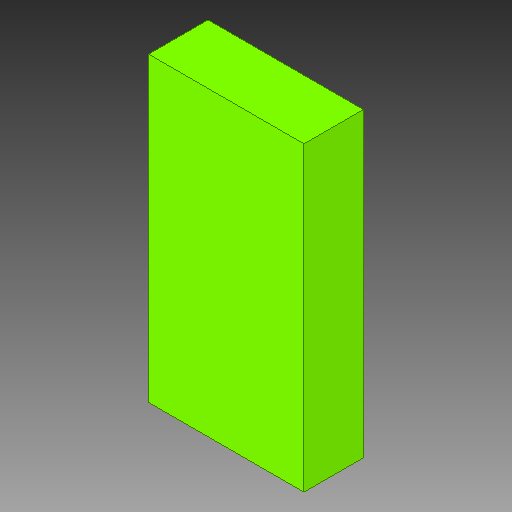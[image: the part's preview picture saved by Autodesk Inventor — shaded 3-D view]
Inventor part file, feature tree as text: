
AUTODESK INVENTOR PART (.ipt)
format: ipt  version: 2018 (Build 220112000, 112)  size: 79,872 bytes
history: native  units: in
note: dims shown in document units (in); Inventor stores cm internally (conversion verified against a paired STEP export)
features: other x1, extrude x1
ambient origin geometry x8: Origin, YZ Plane, XZ Plane, XY Plane, X Axis, Y Axis, Z Axis, Center Point
bodies: Solid1 (feature_tree)
feature tree (2):
  other  "JP1M, CTS_75"
  extrude  "Extrusion1"  Depth=0.0394in TaperAngle=0.0deg
